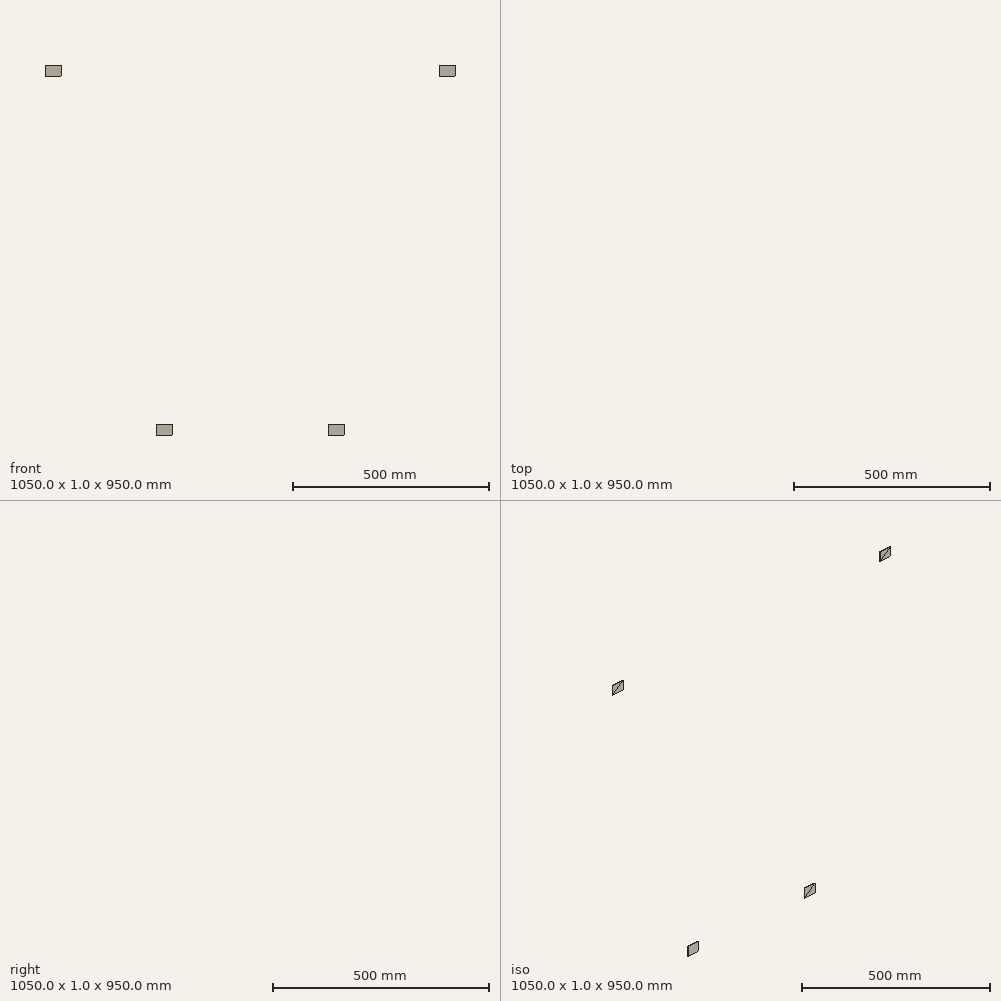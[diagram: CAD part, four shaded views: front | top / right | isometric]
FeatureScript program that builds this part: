
annotation { "Feature Type Name" : "Feature", "Feature Type Description" : "" }
export const myFeature = defineFeature(function(context is Context, id is Id, definition is map)
    precondition{}
    {
        {
            var Q0;
            Q0=qCreatedBy(makeId("Front.planeOp"),FACE);
            var sketch = newSketch(context, id + "F0", { "sketchPlane" : qUnion([Q0])});
            skLineSegment(sketch, "E0.bottom", {"start": v(-525, 460) * mm, "end": v(-485, 460) * mm});
            skLineSegment(sketch, "E0.top", {"start": v(-525, 430) * mm, "end": v(-485, 430) * mm});
            skLineSegment(sketch, "E0.left", {"start": v(-525, 460) * mm, "end": v(-525, 430) * mm});
            skLineSegment(sketch, "E0.right", {"start": v(-485, 460) * mm, "end": v(-485, 430) * mm});
            skLineSegment(sketch, "E1.bottom", {"start": v(485, 460) * mm, "end": v(525, 460) * mm});
            skLineSegment(sketch, "E1.top", {"start": v(485, 430) * mm, "end": v(525, 430) * mm});
            skLineSegment(sketch, "E1.left", {"start": v(485, 460) * mm, "end": v(485, 430) * mm});
            skLineSegment(sketch, "E1.right", {"start": v(525, 460) * mm, "end": v(525, 430) * mm});
            skLineSegment(sketch, "E2.bottom", {"start": v(-240, -460) * mm, "end": v(-200, -460) * mm});
            skLineSegment(sketch, "E2.top", {"start": v(-240, -490) * mm, "end": v(-200, -490) * mm});
            skLineSegment(sketch, "E2.left", {"start": v(-240, -460) * mm, "end": v(-240, -490) * mm});
            skLineSegment(sketch, "E2.right", {"start": v(-200, -460) * mm, "end": v(-200, -490) * mm});
            skLineSegment(sketch, "E3.bottom", {"start": v(200, -460) * mm, "end": v(240, -460) * mm});
            skLineSegment(sketch, "E3.top", {"start": v(200, -490) * mm, "end": v(240, -490) * mm});
            skLineSegment(sketch, "E3.left", {"start": v(200, -460) * mm, "end": v(200, -490) * mm});
            skLineSegment(sketch, "E3.right", {"start": v(240, -460) * mm, "end": v(240, -490) * mm});
            skSolve(sketch);
        }
        {
            var Q0;
            Q0 = qSketchRegion(id + "F0", true);
            extrude(context, id + "F1", {"entities" : qUnion([Q0]), "depth" : 1 * mm, "offsetDistance" : 25 * mm});
        }
    });
